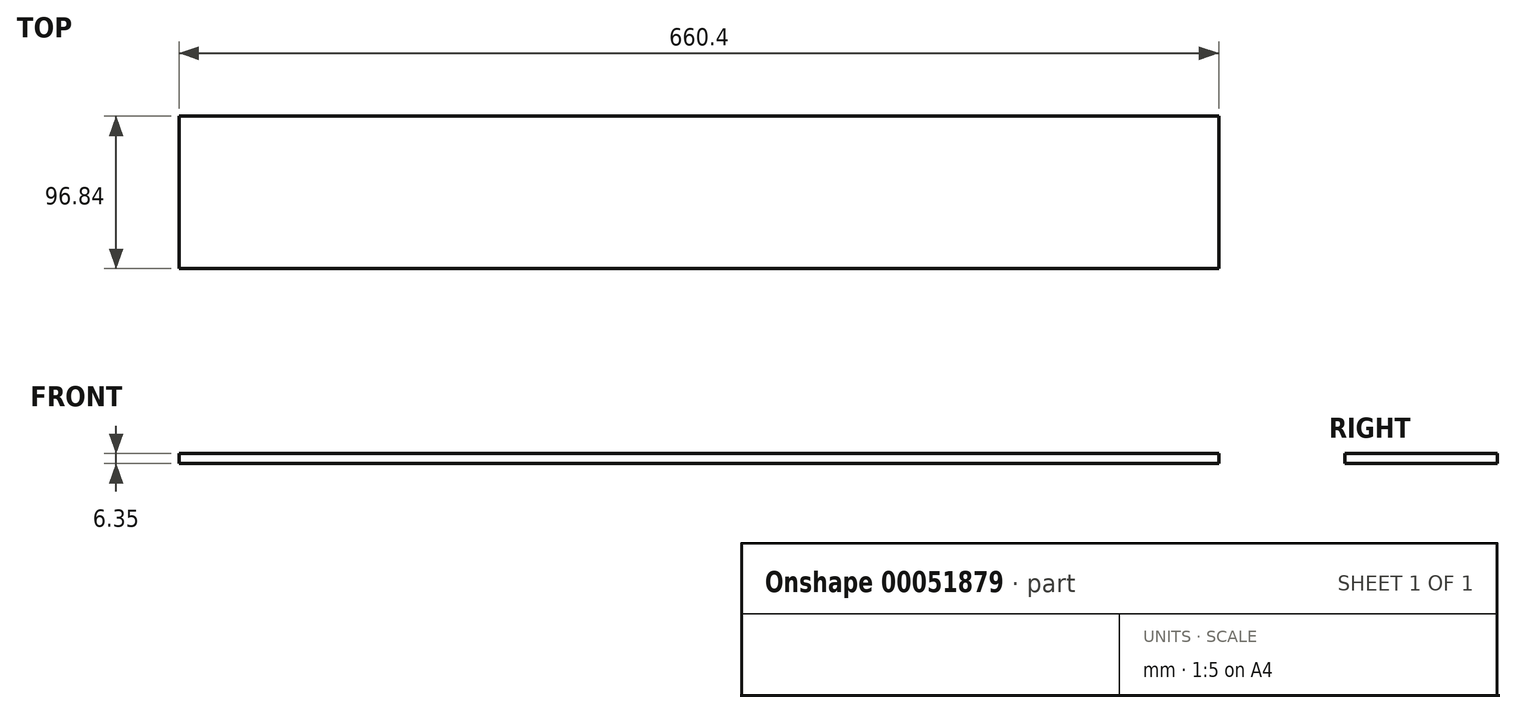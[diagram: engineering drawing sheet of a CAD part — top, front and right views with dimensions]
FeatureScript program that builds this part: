
annotation { "Feature Type Name" : "Feature", "Feature Type Description" : "" }
export const myFeature = defineFeature(function(context is Context, id is Id, definition is map)
    precondition{}
    {
        {
            var Q0;
            Q0=qCreatedBy(makeId("Top.planeOp"),FACE);
            var sketch = newSketch(context, id + "F0", { "sketchPlane" : qUnion([Q0])});
            skLineSegment(sketch, "E0.bottom", {"start": v(-330.2, 50.8) * mm, "end": v(330.2, 50.8) * mm});
            skLineSegment(sketch, "E0.top", {"start": v(-330.2, -46.04) * mm, "end": v(330.2, -46.04) * mm});
            skLineSegment(sketch, "E0.left", {"start": v(-330.2, 50.8) * mm, "end": v(-330.2, -46.04) * mm});
            skLineSegment(sketch, "E0.right", {"start": v(330.2, 50.8) * mm, "end": v(330.2, -46.04) * mm});
            skSolve(sketch);
        }
        {
            var Q0;
            Q0=makeQuery(id+"F0.imprint","IMPRINT",FACE,{"disambiguationData":[TD([[makeQuery(id+"F0.imprint","IMPRINT",EDGE,{"derivedFrom":sQuery(id+"F0.wireOp",EDGE,"E0.bottom")}),-1.0]])]});
            extrude(context, id + "F1", {"entities" : qUnion([Q0]), "depth" : 6.35 * mm});
        }
    });
